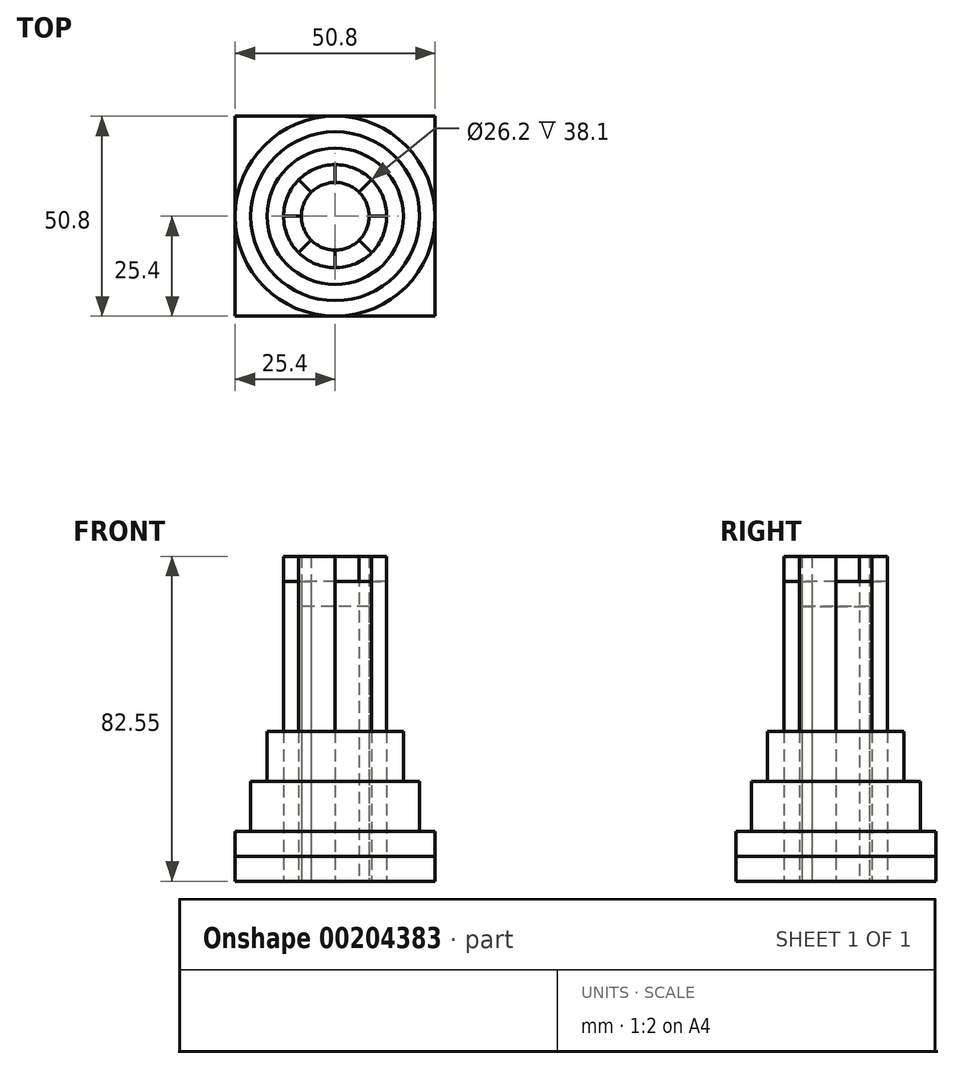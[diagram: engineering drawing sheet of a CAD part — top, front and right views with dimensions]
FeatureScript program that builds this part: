
annotation { "Feature Type Name" : "Feature", "Feature Type Description" : "" }
export const myFeature = defineFeature(function(context is Context, id is Id, definition is map)
    precondition{}
    {
        {
            var Q0;
            Q0=qCreatedBy(makeId("Top.planeOp"),FACE);
            var sketch = newSketch(context, id + "F0", { "sketchPlane" : qUnion([Q0])});
            skLineSegment(sketch, "E0.bottom", {"start": v(25.4, 25.4) * mm, "end": v(-25.4, 25.4) * mm});
            skLineSegment(sketch, "E0.top", {"start": v(25.4, -25.4) * mm, "end": v(-25.4, -25.4) * mm});
            skLineSegment(sketch, "E0.left", {"start": v(25.4, 25.4) * mm, "end": v(25.4, -25.4) * mm});
            skLineSegment(sketch, "E0.right", {"start": v(-25.4, 25.4) * mm, "end": v(-25.4, -25.4) * mm});
            skPoint(sketch, "E0.middle", {"position": v(0, 0) * mm});
            skCircle(sketch, "E1", {"center": v(0, 0) * mm, "radius": 25.4 * mm});
            skCircle(sketch, "E2", {"center": v(0, 0) * mm, "radius": 17.31 * mm});
            skCircle(sketch, "E3", {"center": v(0, 0) * mm, "radius": 13.1 * mm});
            skCircle(sketch, "E4", {"center": v(0, 0) * mm, "radius": 21.46 * mm});
            skCircle(sketch, "E5", {"center": v(0, 0) * mm, "radius": 8.6 * mm});
            skLineSegment(sketch, "E6", {"start": v(0, 8.6) * mm, "end": v(0, 13.1) * mm});
            skLineSegment(sketch, "E7", {"start": v(0, -8.6) * mm, "end": v(0, -13.1) * mm});
            skLineSegment(sketch, "E8", {"start": v(-8.6, 0) * mm, "end": v(-13.1, 0) * mm});
            skLineSegment(sketch, "E9", {"start": v(8.6, 0) * mm, "end": v(13.1, 0) * mm});
            skLineSegment(sketch, "E10", {"start": v(-9.26, 9.26) * mm, "end": v(-6.08, 6.08) * mm});
            skLineSegment(sketch, "E11", {"start": v(9.26, 9.26) * mm, "end": v(6.08, 6.08) * mm});
            skLineSegment(sketch, "E12", {"start": v(-9.26, -9.26) * mm, "end": v(-6.08, -6.08) * mm});
            skLineSegment(sketch, "E13", {"start": v(9.26, -9.26) * mm, "end": v(6.08, -6.08) * mm});
            skSolve(sketch);
        }
        {
            var Q0;
            {var subQ0=sQuery(id+"F0.wireOp",EDGE,"E0.right");var subQ1=sQuery(id+"F0.wireOp",EDGE,"E0.top");var subQ2=makeQuery(id+"F0.imprint","INTERSECT",VERTEX,{"derivedFrom":[subQ1,subQ0]});Q0=makeQuery(id+"F0.imprint","IMPRINT",FACE,{"disambiguationData":[TD([[makeQuery(id+"F0.imprint","IMPRINT",EDGE,{"disambiguationData":[TD([[subQ2,1.0]])],"derivedFrom":subQ1}),-1.0]])]});}
            var Q1;
            {var subQ0=sQuery(id+"F0.wireOp",EDGE,"E0.right");var subQ1=sQuery(id+"F0.wireOp",EDGE,"E0.bottom");var subQ2=makeQuery(id+"F0.imprint","INTERSECT",VERTEX,{"derivedFrom":[subQ1,subQ0]});Q1=makeQuery(id+"F0.imprint","IMPRINT",FACE,{"disambiguationData":[TD([[makeQuery(id+"F0.imprint","IMPRINT",EDGE,{"disambiguationData":[TD([[subQ2,1.0]])],"derivedFrom":subQ1}),1.0]])]});}
            var Q2;
            {var subQ0=sQuery(id+"F0.wireOp",EDGE,"E0.left");var subQ1=sQuery(id+"F0.wireOp",EDGE,"E0.bottom");var subQ2=makeQuery(id+"F0.imprint","INTERSECT",VERTEX,{"derivedFrom":[subQ1,subQ0]});Q2=makeQuery(id+"F0.imprint","IMPRINT",FACE,{"disambiguationData":[TD([[makeQuery(id+"F0.imprint","IMPRINT",EDGE,{"disambiguationData":[TD([[subQ2,-1.0]])],"derivedFrom":subQ1}),1.0]])]});}
            var Q3;
            {var subQ0=sQuery(id+"F0.wireOp",EDGE,"E0.left");var subQ1=sQuery(id+"F0.wireOp",EDGE,"E0.top");var subQ2=makeQuery(id+"F0.imprint","INTERSECT",VERTEX,{"derivedFrom":[subQ1,subQ0]});Q3=makeQuery(id+"F0.imprint","IMPRINT",FACE,{"disambiguationData":[TD([[makeQuery(id+"F0.imprint","IMPRINT",EDGE,{"disambiguationData":[TD([[subQ2,-1.0]])],"derivedFrom":subQ1}),-1.0]])]});}
            extrude(context, id + "F1", {"entities" : qUnion([Q0, Q1, Q2, Q3]), "depth" : 6.35 * mm});
        }
        {
            var Q0;
            Q0=makeQuery(id+"F0.imprint","IMPRINT",FACE,{"disambiguationData":[TD([[makeQuery(id+"F0.imprint","IMPRINT",EDGE,{"derivedFrom":sQuery(id+"F0.wireOp",EDGE,"E4")}),-1.0]])]});
            extrude(context, id + "F2", {"entities" : qUnion([Q0]), "operationType" : NewBodyOperationType.ADD, "depth" : 12.7 * mm});
        }
        {
            var Q0;
            Q0=makeQuery(id+"F0.imprint","IMPRINT",FACE,{"disambiguationData":[TD([[makeQuery(id+"F0.imprint","IMPRINT",EDGE,{"derivedFrom":sQuery(id+"F0.wireOp",EDGE,"E2")}),-1.0]])]});
            extrude(context, id + "F3", {"entities" : qUnion([Q0]), "operationType" : NewBodyOperationType.ADD, "depth" : 25.4 * mm});
        }
        {
            var Q0;
            Q0=makeQuery(id+"F0.imprint","IMPRINT",FACE,{"disambiguationData":[TD([[makeQuery(id+"F0.imprint","IMPRINT",EDGE,{"derivedFrom":sQuery(id+"F0.wireOp",EDGE,"E2")}),1.0]])]});
            extrude(context, id + "F4", {"entities" : qUnion([Q0]), "operationType" : NewBodyOperationType.ADD, "depth" : 38.1 * mm});
        }
        {
            var Q0;
            {var subQ0=sQuery(id+"F0.wireOp",EDGE,"E5");var subQ5=makeQuery(id+"F0.imprint","INTERSECT",VERTEX,{"derivedFrom":[subQ0,sQuery(id+"F0.wireOp",EDGE,"E9")]});Q0=makeQuery(id+"F0.imprint","IMPRINT",FACE,{"disambiguationData":[TD([[makeQuery(id+"F0.imprint","IMPRINT",EDGE,{"disambiguationData":[TD([[subQ5,-1.0]])],"derivedFrom":subQ0}),1.0]])]});}
            extrude(context, id + "F5", {"entities" : qUnion([Q0]), "depth" : 69.85 * mm});
        }
        {
            var Q0;
            {var subQ0=sQuery(id+"F0.wireOp",EDGE,"E6");Q0=makeQuery(id+"F0.imprint","IMPRINT",FACE,{"disambiguationData":[TD([[makeQuery(id+"F0.imprint","IMPRINT",EDGE,{"derivedFrom":subQ0}),1.0]])]});}
            var Q1;
            {var subQ0=sQuery(id+"F0.wireOp",EDGE,"E9");Q1=makeQuery(id+"F0.imprint","IMPRINT",FACE,{"disambiguationData":[TD([[makeQuery(id+"F0.imprint","IMPRINT",EDGE,{"derivedFrom":subQ0}),1.0]])]});}
            var Q2;
            {var subQ0=sQuery(id+"F0.wireOp",EDGE,"E7");Q2=makeQuery(id+"F0.imprint","IMPRINT",FACE,{"disambiguationData":[TD([[makeQuery(id+"F0.imprint","IMPRINT",EDGE,{"derivedFrom":subQ0}),1.0]])]});}
            var Q3;
            {var subQ0=sQuery(id+"F0.wireOp",EDGE,"E8");Q3=makeQuery(id+"F0.imprint","IMPRINT",FACE,{"disambiguationData":[TD([[makeQuery(id+"F0.imprint","IMPRINT",EDGE,{"derivedFrom":subQ0}),1.0]])]});}
            extrude(context, id + "F6", {"entities" : qUnion([Q0, Q1, Q2, Q3]), "depth" : 76.2 * mm});
        }
        {
            var Q0;
            {var subQ0=sQuery(id+"F0.wireOp",EDGE,"E8");Q0=makeQuery(id+"F0.imprint","IMPRINT",FACE,{"disambiguationData":[TD([[makeQuery(id+"F0.imprint","IMPRINT",EDGE,{"derivedFrom":subQ0}),-1.0]])]});}
            var Q1;
            {var subQ0=sQuery(id+"F0.wireOp",EDGE,"E6");Q1=makeQuery(id+"F0.imprint","IMPRINT",FACE,{"disambiguationData":[TD([[makeQuery(id+"F0.imprint","IMPRINT",EDGE,{"derivedFrom":subQ0}),-1.0]])]});}
            var Q2;
            {var subQ0=sQuery(id+"F0.wireOp",EDGE,"E9");Q2=makeQuery(id+"F0.imprint","IMPRINT",FACE,{"disambiguationData":[TD([[makeQuery(id+"F0.imprint","IMPRINT",EDGE,{"derivedFrom":subQ0}),-1.0]])]});}
            var Q3;
            {var subQ0=sQuery(id+"F0.wireOp",EDGE,"E7");Q3=makeQuery(id+"F0.imprint","IMPRINT",FACE,{"disambiguationData":[TD([[makeQuery(id+"F0.imprint","IMPRINT",EDGE,{"derivedFrom":subQ0}),-1.0]])]});}
            extrude(context, id + "F7", {"entities" : qUnion([Q0, Q1, Q2, Q3]), "depth" : 82.55 * mm});
        }
    });
